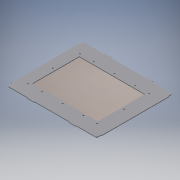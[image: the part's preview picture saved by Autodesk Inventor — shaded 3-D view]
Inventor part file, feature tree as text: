
AUTODESK INVENTOR PART (.ipt)
format: ipt  version: 2018 (Build 220112000, 112)  size: 286,720 bytes
history: native  units: mm
features: reference x12, other x7, sketch x2, plane x1, extrude x1, projected_geometry x1
ambient origin geometry x8: Origin, YZ Plane, XZ Plane, XY Plane, X Axis, Y Axis, Z Axis, Center Point
bodies: Volumenkörper1 (feature_tree)
feature tree (24):
  plane  "Arbeitsebene1"
  other  "Fläche1"
  extrude  "Extrusion1"  Depth=190.0mm
  sketch  "Skizze1"  dims[d0=0.05mm d1=190.0mm]
  reference  "Referenz1"
  reference  "Referenz2"
  reference  "Referenz3"
  reference  "Referenz4"
  reference  "Referenz5"
  reference  "Referenz6"
  reference  "Referenz7"
  reference  "Referenz8"
  reference  "Referenz9"
  reference  "Referenz10"
  reference  "Referenz11"
  other  "Grobblech1"
  reference  "Referenz12"
  sketch  "Skizze2"  dims[d2=136.0mm d3=2.0mm d4=8.0mm d5=8.0mm d6=8.0mm d7=8.0mm d8=10.0mm d9=0.0mm]
  projected_geometry  "Projizierte Kontur1"
  parser-record x1  (decoder bookkeeping rows leaked as tree rows — omitted from the tree; the rows remain in map.json)
  other  "Montiert.iam"
  other  "Gegenhalter:1"
  other  "Definition1"
  other  "Brenner:1"
note: 1 file-system path scrubbed to <path> (originals preserved in map.json)
